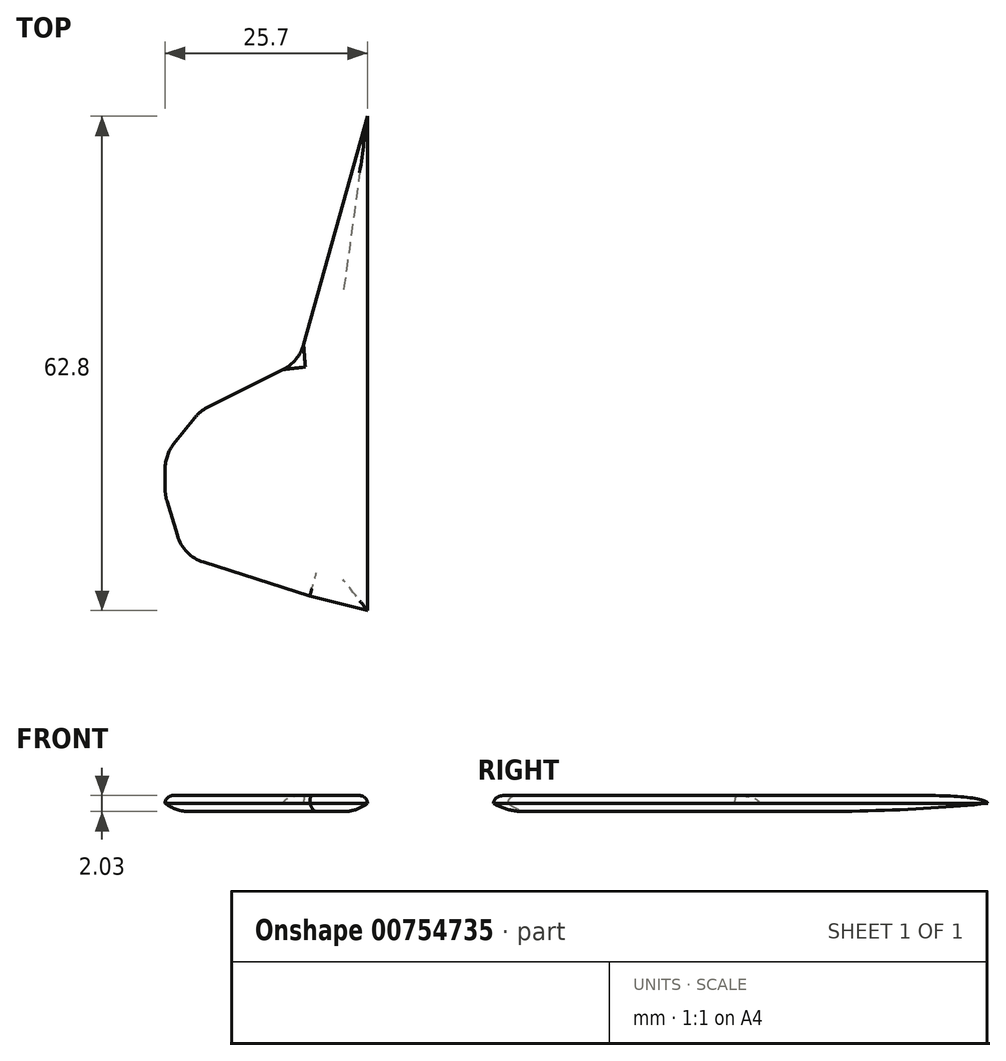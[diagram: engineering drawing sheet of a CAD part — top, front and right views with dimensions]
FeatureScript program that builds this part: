
annotation { "Feature Type Name" : "Feature", "Feature Type Description" : "" }
export const myFeature = defineFeature(function(context is Context, id is Id, definition is map)
    precondition{}
    {
        {
            var Q0;
            Q0=qCreatedBy(makeId("Top.planeOp"),FACE);
            var sketch = newSketch(context, id + "F0", { "sketchPlane" : qUnion([Q0])});
            skLineSegment(sketch, "E0", {"start": v(0, 50.59) * mm, "end": v(-8.72, 19.42) * mm});
            skLineSegment(sketch, "E1", {"start": v(-8.72, 19.42) * mm, "end": v(-21.28, 13.14) * mm});
            skLineSegment(sketch, "E2", {"start": v(-21.28, 13.14) * mm, "end": v(-25.7, 7.56) * mm});
            skLineSegment(sketch, "E3", {"start": v(-25.7, 7.56) * mm, "end": v(-25.7, 2.44) * mm});
            skLineSegment(sketch, "E4", {"start": v(-25.7, 2.44) * mm, "end": v(-23.38, -5.23) * mm});
            skLineSegment(sketch, "E5", {"start": v(-23.38, -5.23) * mm, "end": v(-7.33, -10.35) * mm});
            skLineSegment(sketch, "E6", {"start": v(-7.33, -10.35) * mm, "end": v(0, -12.21) * mm});
            skLineSegment(sketch, "E7", {"start": v(0, -12.21) * mm, "end": v(0, 50.59) * mm});
            skSolve(sketch);
        }
        {
            var Q0;
            Q0=makeQuery(id+"F0.imprint","IMPRINT",FACE,{"disambiguationData":[TD([[makeQuery(id+"F0.imprint","IMPRINT",EDGE,{"derivedFrom":sQuery(id+"F0.wireOp",EDGE,"E0")}),1.0]])]});
            extrude(context, id + "F1", {"entities" : qUnion([Q0]), "depth" : 2.03 * mm, "offsetDistance" : 25.4 * mm});
        }
        {
            var Q0;
            Q0=makeQuery(id+"F1.opExtrude","CAP_FACE",FACE,{"disambiguationData":[OSD([sQuery(id+"F0.wireOp",EDGE,"E0"),sQuery(id+"F0.wireOp",EDGE,"E1"),sQuery(id+"F0.wireOp",EDGE,"E2"),sQuery(id+"F0.wireOp",EDGE,"E3"),sQuery(id+"F0.wireOp",EDGE,"E4"),sQuery(id+"F0.wireOp",EDGE,"E5"),sQuery(id+"F0.wireOp",EDGE,"E6"),sQuery(id+"F0.wireOp",EDGE,"E7")])],"isStart":false});
            fillet(context, id + "F2", {"entities" : qUnion([Q0]), "radius" : 0.98 * mm, "tangentPropagation" : true, "allowEdgeOverflow" : false});
        }
        {
            var Q0;
            Q0=makeQuery(id+"F2.opFillet","BLEND_EDGE",EDGE,{"blendedFrom":[makeQuery(id+"F1.opExtrude","CAP_EDGE",EDGE,{"disambiguationData":[OSD([sQuery(id+"F0.wireOp",EDGE,"E1")])],"isStart":false}),makeQuery(id+"F1.opExtrude","CAP_EDGE",EDGE,{"disambiguationData":[OSD([sQuery(id+"F0.wireOp",EDGE,"E2")])],"isStart":false})],"blendedInto":[]});
            var Q1;
            Q1=makeQuery(id+"F1.opExtrude","SWEPT_EDGE",EDGE,{"disambiguationData":[OSD([sQuery(id+"F0.wireOp",EDGE,"E1"),sQuery(id+"F0.wireOp",EDGE,"E2")])]});
            var Q2;
            Q2=makeQuery(id+"F1.opExtrude","SWEPT_EDGE",EDGE,{"disambiguationData":[OSD([sQuery(id+"F0.wireOp",EDGE,"E2"),sQuery(id+"F0.wireOp",EDGE,"E3")])]});
            var Q3;
            Q3=makeQuery(id+"F2.opFillet","BLEND_EDGE",EDGE,{"blendedFrom":[makeQuery(id+"F1.opExtrude","CAP_EDGE",EDGE,{"disambiguationData":[OSD([sQuery(id+"F0.wireOp",EDGE,"E2")])],"isStart":false}),makeQuery(id+"F1.opExtrude","CAP_EDGE",EDGE,{"disambiguationData":[OSD([sQuery(id+"F0.wireOp",EDGE,"E3")])],"isStart":false})],"blendedInto":[]});
            var Q4;
            Q4=makeQuery(id+"F1.opExtrude","SWEPT_EDGE",EDGE,{"disambiguationData":[OSD([sQuery(id+"F0.wireOp",EDGE,"E3"),sQuery(id+"F0.wireOp",EDGE,"E4")])]});
            var Q5;
            Q5=makeQuery(id+"F2.opFillet","BLEND_EDGE",EDGE,{"blendedFrom":[makeQuery(id+"F1.opExtrude","CAP_EDGE",EDGE,{"disambiguationData":[OSD([sQuery(id+"F0.wireOp",EDGE,"E3")])],"isStart":false}),makeQuery(id+"F1.opExtrude","CAP_EDGE",EDGE,{"disambiguationData":[OSD([sQuery(id+"F0.wireOp",EDGE,"E4")])],"isStart":false})],"blendedInto":[]});
            var Q6;
            Q6=makeQuery(id+"F1.opExtrude","SWEPT_EDGE",EDGE,{"disambiguationData":[OSD([sQuery(id+"F0.wireOp",EDGE,"E4"),sQuery(id+"F0.wireOp",EDGE,"E5")])]});
            var Q7;
            Q7=makeQuery(id+"F2.opFillet","BLEND_EDGE",EDGE,{"blendedFrom":[makeQuery(id+"F1.opExtrude","CAP_EDGE",EDGE,{"disambiguationData":[OSD([sQuery(id+"F0.wireOp",EDGE,"E4")])],"isStart":false}),makeQuery(id+"F1.opExtrude","CAP_EDGE",EDGE,{"disambiguationData":[OSD([sQuery(id+"F0.wireOp",EDGE,"E5")])],"isStart":false})],"blendedInto":[]});
            var Q8;
            Q8=makeQuery(id+"F2.opFillet","BLEND_EDGE",EDGE,{"blendedFrom":[makeQuery(id+"F1.opExtrude","CAP_EDGE",EDGE,{"disambiguationData":[OSD([sQuery(id+"F0.wireOp",EDGE,"E0")])],"isStart":false}),makeQuery(id+"F1.opExtrude","CAP_EDGE",EDGE,{"disambiguationData":[OSD([sQuery(id+"F0.wireOp",EDGE,"E1")])],"isStart":false})],"blendedInto":[]});
            var Q9;
            Q9=makeQuery(id+"F1.opExtrude","SWEPT_EDGE",EDGE,{"disambiguationData":[OSD([sQuery(id+"F0.wireOp",EDGE,"E0"),sQuery(id+"F0.wireOp",EDGE,"E1")])]});
            fillet(context, id + "F3", {"entities" : qUnion([Q0, Q1, Q2, Q3, Q4, Q5, Q6, Q7, Q8, Q9]), "radius" : 5.08 * mm, "tangentPropagation" : true, "allowEdgeOverflow" : false});
        }
        {
            var Q0;
            Q0=makeQuery(id+"F1.opExtrude","CAP_FACE",FACE,{"disambiguationData":[OSD([sQuery(id+"F0.wireOp",EDGE,"E0"),sQuery(id+"F0.wireOp",EDGE,"E1"),sQuery(id+"F0.wireOp",EDGE,"E2"),sQuery(id+"F0.wireOp",EDGE,"E3"),sQuery(id+"F0.wireOp",EDGE,"E4"),sQuery(id+"F0.wireOp",EDGE,"E5"),sQuery(id+"F0.wireOp",EDGE,"E6"),sQuery(id+"F0.wireOp",EDGE,"E7")])],"isStart":true});
            fillet(context, id + "F4", {"entities" : qUnion([Q0]), "radius" : 5.08 * mm, "tangentPropagation" : true, "allowEdgeOverflow" : false});
        }
    });
